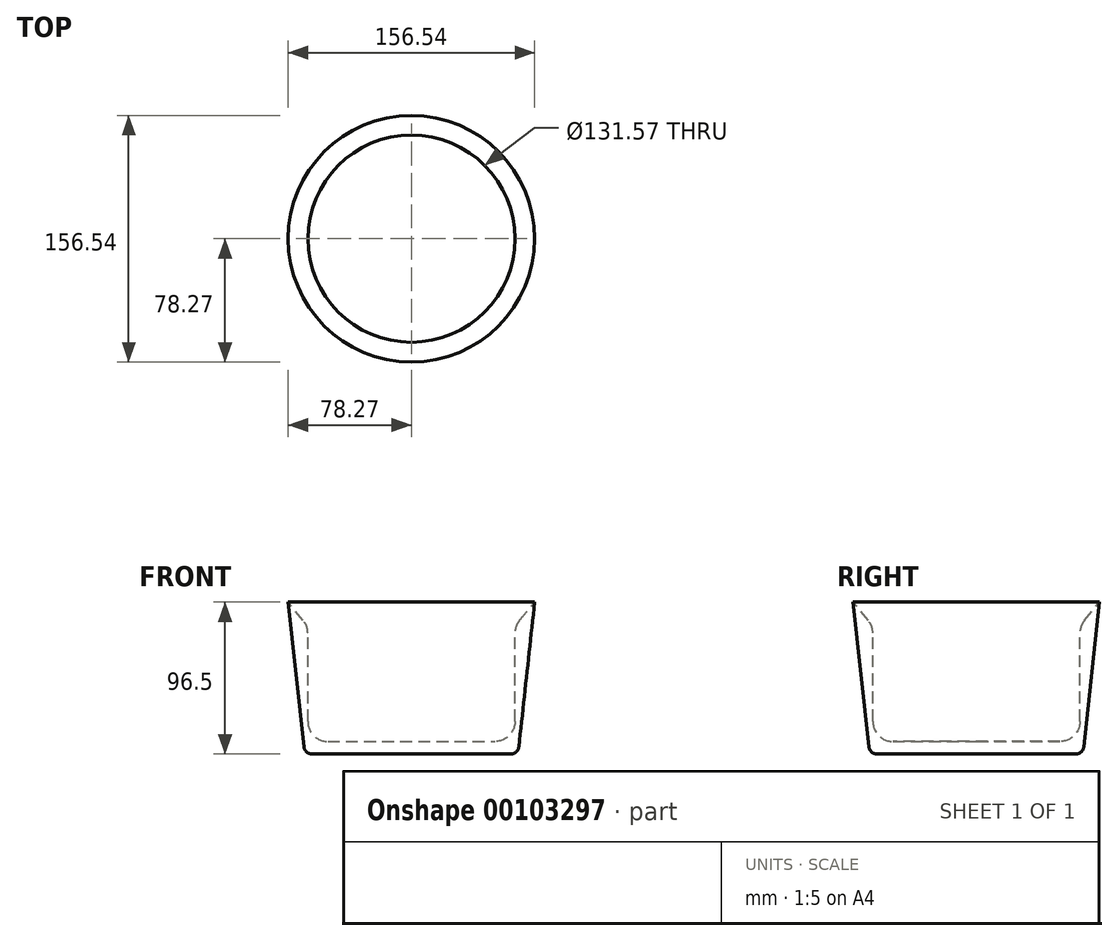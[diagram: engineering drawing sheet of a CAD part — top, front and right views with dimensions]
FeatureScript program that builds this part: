
annotation { "Feature Type Name" : "Feature", "Feature Type Description" : "" }
export const myFeature = defineFeature(function(context is Context, id is Id, definition is map)
    precondition{}
    {
        {
            var Q0;
            Q0=qCreatedBy(makeId("Right.planeOp"),FACE);
            var sketch = newSketch(context, id + "F0", { "sketchPlane" : qUnion([Q0])});
            skLineSegment(sketch, "E0", {"start": v(-78.27, 60.01) * mm, "end": v(-65.79, 44.88) * mm});
            skLineSegment(sketch, "E1", {"start": v(-65.79, 44.88) * mm, "end": v(-65.79, -28.5) * mm});
            skLineSegment(sketch, "E2", {"start": v(-65.79, -28.5) * mm, "end": v(0, -28.5) * mm});
            skLineSegment(sketch, "E3", {"start": v(0, -28.5) * mm, "end": v(0, -36.49) * mm});
            skLineSegment(sketch, "E4", {"start": v(0, -36.49) * mm, "end": v(-67.73, -36.49) * mm});
            skLineSegment(sketch, "E5", {"start": v(-67.73, -36.49) * mm, "end": v(-78.27, 60.01) * mm});
            skSolve(sketch);
        }
        {
            var Q0;
            Q0=makeQuery(id+"F0.imprint","IMPRINT",FACE,{"disambiguationData":[TD([[makeQuery(id+"F0.imprint","IMPRINT",EDGE,{"derivedFrom":sQuery(id+"F0.wireOp",EDGE,"E0")}),-1.0]])]});
            var Q1;
            Q1=sQuery(id+"F0.wireOp",EDGE,"E3");
            revolve(context, id + "F1", {"entities" : qUnion([Q0]), "axis" : qUnion([Q1]), "revolveType" : RevolveType.FULL});
        }
        {
            var Q0;
            Q0=makeQuery(id+"F1.opRevolve","SWEPT_FACE",FACE,{"disambiguationData":[OSD([sQuery(id+"F0.wireOp",EDGE,"E1")])]});
            fillet(context, id + "F2", {"entities" : qUnion([Q0]), "radius" : 12.7 * mm, "tangentPropagation" : true, "allowEdgeOverflow" : false});
        }
        {
            var Q0;
            Q0=makeQuery(id+"F1.opRevolve","SWEPT_FACE",FACE,{"disambiguationData":[OSD([sQuery(id+"F0.wireOp",EDGE,"E4")])]});
            fillet(context, id + "F3", {"entities" : qUnion([Q0]), "radius" : 5.08 * mm, "tangentPropagation" : true, "allowEdgeOverflow" : false});
        }
    });
